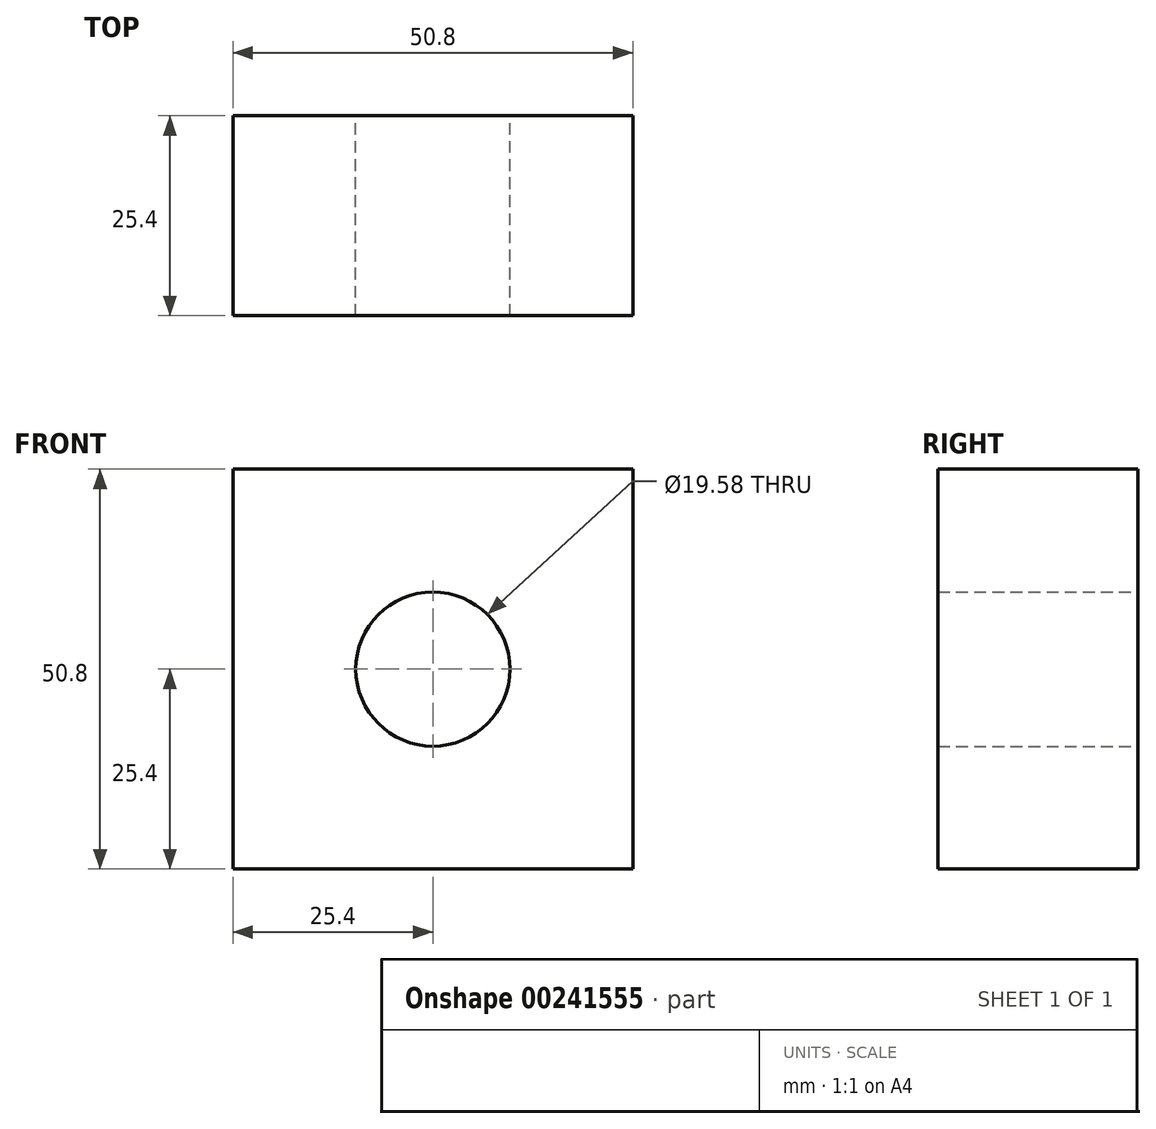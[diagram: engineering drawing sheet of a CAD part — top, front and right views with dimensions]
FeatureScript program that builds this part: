
annotation { "Feature Type Name" : "Feature", "Feature Type Description" : "" }
export const myFeature = defineFeature(function(context is Context, id is Id, definition is map)
    precondition{}
    {
        {
            var Q0;
            Q0=qCreatedBy(makeId("Front.planeOp"),FACE);
            var sketch = newSketch(context, id + "F0", { "sketchPlane" : qUnion([Q0])});
            skLineSegment(sketch, "E0.bottom", {"start": v(25.4, 25.4) * mm, "end": v(-25.4, 25.4) * mm});
            skLineSegment(sketch, "E0.top", {"start": v(25.4, -25.4) * mm, "end": v(-25.4, -25.4) * mm});
            skLineSegment(sketch, "E0.left", {"start": v(25.4, 25.4) * mm, "end": v(25.4, -25.4) * mm});
            skLineSegment(sketch, "E0.right", {"start": v(-25.4, 25.4) * mm, "end": v(-25.4, -25.4) * mm});
            skPoint(sketch, "E0.middle", {"position": v(0, 0) * mm});
            skCircle(sketch, "E1", {"center": v(0, 0) * mm, "radius": 9.79 * mm});
            skSolve(sketch);
        }
        {
            var Q0;
            Q0=makeQuery(id+"F0.imprint","IMPRINT",FACE,{"disambiguationData":[TD([[makeQuery(id+"F0.imprint","IMPRINT",EDGE,{"derivedFrom":sQuery(id+"F0.wireOp",EDGE,"E0.bottom")}),1.0]])]});
            extrude(context, id + "F1", {"entities" : qUnion([Q0]), "depth" : 25.4 * mm});
        }
    });
